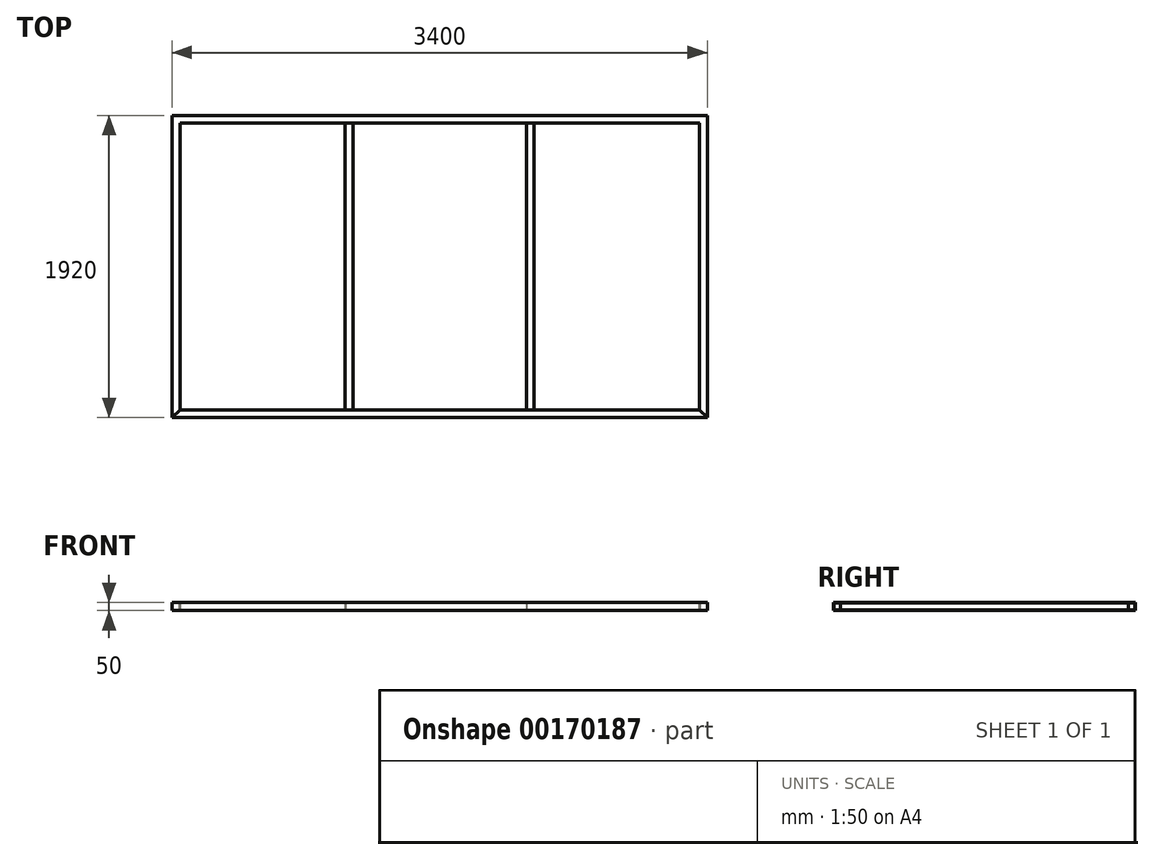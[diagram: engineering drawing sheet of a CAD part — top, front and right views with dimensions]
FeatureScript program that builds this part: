
annotation { "Feature Type Name" : "Feature", "Feature Type Description" : "" }
export const myFeature = defineFeature(function(context is Context, id is Id, definition is map)
    precondition{}
    {
        {
            var Q0;
            Q0=qCreatedBy(makeId("Right.planeOp"),FACE);
            var sketch = newSketch(context, id + "F0", { "sketchPlane" : qUnion([Q0])});
            skLineSegment(sketch, "E0", {"start": v(-910, 0) * mm, "end": v(910, 0) * mm});
            skLineSegment(sketch, "E1.bottom", {"start": v(-910, 0) * mm, "end": v(-960, 0) * mm});
            skLineSegment(sketch, "E1.top", {"start": v(-910, 50) * mm, "end": v(-960, 50) * mm});
            skLineSegment(sketch, "E1.left", {"start": v(-910, 0) * mm, "end": v(-910, 50) * mm});
            skLineSegment(sketch, "E2.0", {"start": v(-913, 47) * mm, "end": v(-957, 47) * mm});
            skLineSegment(sketch, "E2.1", {"start": v(-913, 3) * mm, "end": v(-913, 47) * mm});
            skLineSegment(sketch, "E2.2", {"start": v(-913, 3) * mm, "end": v(-957, 3) * mm});
            skLineSegment(sketch, "E3", {"start": v(0, 0) * mm, "end": v(0, 124) * mm, "construction": true});
            skLineSegment(sketch, "E4.MirrorCS", {"start": v(910, 50) * mm, "end": v(960, 50) * mm});
            skLineSegment(sketch, "E5.MirrorCS", {"start": v(910, 0) * mm, "end": v(960, 0) * mm});
            skLineSegment(sketch, "E6.MirrorCS", {"start": v(913, 3) * mm, "end": v(913, 47) * mm});
            skLineSegment(sketch, "E7.MirrorCS", {"start": v(910, 0) * mm, "end": v(910, 50) * mm});
            skLineSegment(sketch, "E8", {"start": v(-960, 50) * mm, "end": v(-960, 0) * mm});
            skLineSegment(sketch, "E9.0", {"start": v(-957, 47) * mm, "end": v(-957, 3) * mm});
            skLineSegment(sketch, "E10.MirrorCS", {"start": v(960, 50) * mm, "end": v(960, 0) * mm});
            skLineSegment(sketch, "E11.MirrorCS", {"start": v(957, 47) * mm, "end": v(957, 3) * mm});
            skLineSegment(sketch, "E12.MirrorCS", {"start": v(913, 47) * mm, "end": v(957, 47) * mm});
            skLineSegment(sketch, "E13.MirrorCS", {"start": v(913, 3) * mm, "end": v(957, 3) * mm});
            skSolve(sketch);
        }
        {
            var Q0;
            Q0 = qSketchRegion(id + "F0", true);
            extrude(context, id + "F1", {"entities" : qUnion([Q0]), "depth" : 3400 * mm});
        }
        {
            var Q0;
            Q0=makeQuery(id+"F1.opExtrude","CAP_EDGE",EDGE,{"disambiguationData":[OSD([sQuery(id+"F0.wireOp",EDGE,"E7.MirrorCS")])],"isStart":false});
            var Q1;
            Q1=makeQuery(id+"F1.opExtrude","CAP_EDGE",EDGE,{"disambiguationData":[OSD([sQuery(id+"F0.wireOp",EDGE,"E1.left")])],"isStart":false});
            var Q2;
            Q2=makeQuery(id+"F1.opExtrude","CAP_EDGE",EDGE,{"disambiguationData":[OSD([sQuery(id+"F0.wireOp",EDGE,"E1.left")])],"isStart":true});
            var Q3;
            Q3=makeQuery(id+"F1.opExtrude","CAP_EDGE",EDGE,{"disambiguationData":[OSD([sQuery(id+"F0.wireOp",EDGE,"E7.MirrorCS")])],"isStart":true});
            chamfer(context, id + "F2", {"entities" : qUnion([Q0, Q1, Q2, Q3]), "width" : 50 * mm});
        }
        {
            var Q0;
            Q0=makeQuery(id+"F1.opExtrude","SWEPT_FACE",FACE,{"disambiguationData":[OSD([sQuery(id+"F0.wireOp",EDGE,"E7.MirrorCS")])]});
            var sketch = newSketch(context, id + "F3", { "sketchPlane" : qUnion([Q0])});
            skLineSegment(sketch, "E14.bottom", {"start": v(3400, 50) * mm, "end": v(3350, 50) * mm});
            skLineSegment(sketch, "E14.top", {"start": v(3400, 0) * mm, "end": v(3350, 0) * mm});
            skLineSegment(sketch, "E14.left", {"start": v(3400, 50) * mm, "end": v(3400, 47) * mm});
            skLineSegment(sketch, "E14.right", {"start": v(3350, 50) * mm, "end": v(3350, 0) * mm});
            skLineSegment(sketch, "E15.bottom", {"start": v(2250, 50) * mm, "end": v(2300, 50) * mm});
            skLineSegment(sketch, "E15.top", {"start": v(2250, 0) * mm, "end": v(2300, 0) * mm});
            skLineSegment(sketch, "E15.left", {"start": v(2250, 50) * mm, "end": v(2250, 0) * mm});
            skLineSegment(sketch, "E15.right", {"start": v(2300, 50) * mm, "end": v(2300, 47) * mm});
            skLineSegment(sketch, "E16.bottom", {"start": v(1100, 50) * mm, "end": v(1150, 50) * mm});
            skLineSegment(sketch, "E16.top", {"start": v(1100, 0) * mm, "end": v(1150, 0) * mm});
            skLineSegment(sketch, "E16.left", {"start": v(1100, 50) * mm, "end": v(1100, 0) * mm});
            skLineSegment(sketch, "E16.right", {"start": v(1150, 50) * mm, "end": v(1150, 47) * mm});
            skLineSegment(sketch, "E17.bottom", {"start": v(0, 0) * mm, "end": v(50, 0) * mm});
            skLineSegment(sketch, "E17.top", {"start": v(0, 50) * mm, "end": v(50, 50) * mm});
            skLineSegment(sketch, "E17.left", {"start": v(0, 0) * mm, "end": v(0, 3) * mm});
            skLineSegment(sketch, "E17.right", {"start": v(50, 0) * mm, "end": v(50, 50) * mm});
            skLineSegment(sketch, "E18.0", {"start": v(3400, 47) * mm, "end": v(3353, 47) * mm});
            skLineSegment(sketch, "E18.2", {"start": v(3400, 3) * mm, "end": v(3353, 3) * mm});
            skLineSegment(sketch, "E18.3", {"start": v(3353, 47) * mm, "end": v(3353, 3) * mm});
            skLineSegment(sketch, "E19.0", {"start": v(2253, 47) * mm, "end": v(2300, 47) * mm});
            skLineSegment(sketch, "E19.1", {"start": v(2253, 47) * mm, "end": v(2253, 3) * mm});
            skLineSegment(sketch, "E19.2", {"start": v(2253, 3) * mm, "end": v(2300, 3) * mm});
            skLineSegment(sketch, "E20.0", {"start": v(1103, 47) * mm, "end": v(1150, 47) * mm});
            skLineSegment(sketch, "E20.1", {"start": v(1103, 47) * mm, "end": v(1103, 3) * mm});
            skLineSegment(sketch, "E20.2", {"start": v(1103, 3) * mm, "end": v(1150, 3) * mm});
            skLineSegment(sketch, "E21.0", {"start": v(0, 47) * mm, "end": v(47, 47) * mm});
            skLineSegment(sketch, "E21.2", {"start": v(0, 3) * mm, "end": v(47, 3) * mm});
            skLineSegment(sketch, "E21.3", {"start": v(47, 3) * mm, "end": v(47, 47) * mm});
            skLineSegment(sketch, "E22.trimOffspring", {"start": v(2300, 3) * mm, "end": v(2300, 0) * mm});
            skLineSegment(sketch, "E23.trimOffspring", {"start": v(1150, 3) * mm, "end": v(1150, 0) * mm});
            skLineSegment(sketch, "E24.trimOffspring", {"start": v(3400, 3) * mm, "end": v(3400, 0) * mm});
            skLineSegment(sketch, "E25.trimOffspring", {"start": v(0, 47) * mm, "end": v(0, 50) * mm});
            skSolve(sketch);
        }
        {
            var Q0;
            Q0 = qSketchRegion(id + "F3", true);
            var Q1;
            Q1=makeQuery(id+"F1.opExtrude","SWEPT_BODY",BODY,{"disambiguationData":[OSD([sQuery(id+"F0.wireOp",EDGE,"E1.bottom"),sQuery(id+"F0.wireOp",EDGE,"E1.top"),sQuery(id+"F0.wireOp",EDGE,"E1.left"),sQuery(id+"F0.wireOp",EDGE,"E2.0"),sQuery(id+"F0.wireOp",EDGE,"E2.1"),sQuery(id+"F0.wireOp",EDGE,"E2.2"),sQuery(id+"F0.wireOp",EDGE,"E8"),sQuery(id+"F0.wireOp",EDGE,"E9.0")])]});
            var Q2;
            Q2=makeQuery(id+"F1.opExtrude","SWEPT_FACE",FACE,{"disambiguationData":[OSD([sQuery(id+"F0.wireOp",EDGE,"E11.MirrorCS")])]});
            extrude(context, id + "F4", {"entities" : qUnion([Q0]), "endBound" : BoundingType.UP_TO_BODY, "endBoundEntityBody" : qUnion([Q1]), "depth" : 25 * mm});
        }
        {
            var Q0;
            Q0=makeQuery(id+"F4.opExtrude","CAP_FACE",FACE,{"disambiguationData":[OSD([sQuery(id+"F3.wireOp",EDGE,"E17.bottom"),sQuery(id+"F3.wireOp",EDGE,"E17.top"),sQuery(id+"F3.wireOp",EDGE,"E17.left"),sQuery(id+"F3.wireOp",EDGE,"E17.right"),sQuery(id+"F3.wireOp",EDGE,"E21.0"),sQuery(id+"F3.wireOp",EDGE,"E21.2"),sQuery(id+"F3.wireOp",EDGE,"E21.3"),sQuery(id+"F3.wireOp",EDGE,"E25.trimOffspring")])],"isStart":true});
            var Q1;
            Q1=makeQuery(id+"F1.opExtrude","SWEPT_FACE",FACE,{"disambiguationData":[OSD([sQuery(id+"F0.wireOp",EDGE,"E10.MirrorCS")])]});
            var Q2;
            Q2=makeQuery(id+"F1.opExtrude","SWEPT_BODY",BODY,{"disambiguationData":[OSD([sQuery(id+"F0.wireOp",EDGE,"E4.MirrorCS"),sQuery(id+"F0.wireOp",EDGE,"E5.MirrorCS"),sQuery(id+"F0.wireOp",EDGE,"E7.MirrorCS"),sQuery(id+"F0.wireOp",EDGE,"E6.MirrorCS"),sQuery(id+"F0.wireOp",EDGE,"E10.MirrorCS"),sQuery(id+"F0.wireOp",EDGE,"E11.MirrorCS"),sQuery(id+"F0.wireOp",EDGE,"E12.MirrorCS"),sQuery(id+"F0.wireOp",EDGE,"E13.MirrorCS")])]});
            extrude(context, id + "F5", {"entities" : qUnion([Q0]), "operationType" : NewBodyOperationType.ADD, "endBound" : BoundingType.UP_TO_BODY, "endBoundEntityFace" : qUnion([Q1]), "endBoundEntityBody" : qUnion([Q2]), "depth" : 25 * mm});
        }
        {
            var Q0;
            Q0=makeQuery(id+"F4.opExtrude","CAP_FACE",FACE,{"disambiguationData":[OSD([sQuery(id+"F3.wireOp",EDGE,"E14.bottom"),sQuery(id+"F3.wireOp",EDGE,"E14.top"),sQuery(id+"F3.wireOp",EDGE,"E14.left"),sQuery(id+"F3.wireOp",EDGE,"E14.right"),sQuery(id+"F3.wireOp",EDGE,"E18.0"),sQuery(id+"F3.wireOp",EDGE,"E18.2"),sQuery(id+"F3.wireOp",EDGE,"E18.3"),sQuery(id+"F3.wireOp",EDGE,"E24.trimOffspring")])],"isStart":true});
            var Q1;
            Q1=makeQuery(id+"F1.opExtrude","SWEPT_BODY",BODY,{"disambiguationData":[OSD([sQuery(id+"F0.wireOp",EDGE,"E4.MirrorCS"),sQuery(id+"F0.wireOp",EDGE,"E5.MirrorCS"),sQuery(id+"F0.wireOp",EDGE,"E7.MirrorCS"),sQuery(id+"F0.wireOp",EDGE,"E6.MirrorCS"),sQuery(id+"F0.wireOp",EDGE,"E10.MirrorCS"),sQuery(id+"F0.wireOp",EDGE,"E11.MirrorCS"),sQuery(id+"F0.wireOp",EDGE,"E12.MirrorCS"),sQuery(id+"F0.wireOp",EDGE,"E13.MirrorCS")])]});
            extrude(context, id + "F6", {"entities" : qUnion([Q0]), "operationType" : NewBodyOperationType.ADD, "endBound" : BoundingType.UP_TO_BODY, "endBoundEntityBody" : qUnion([Q1]), "depth" : 25 * mm});
        }
    });
